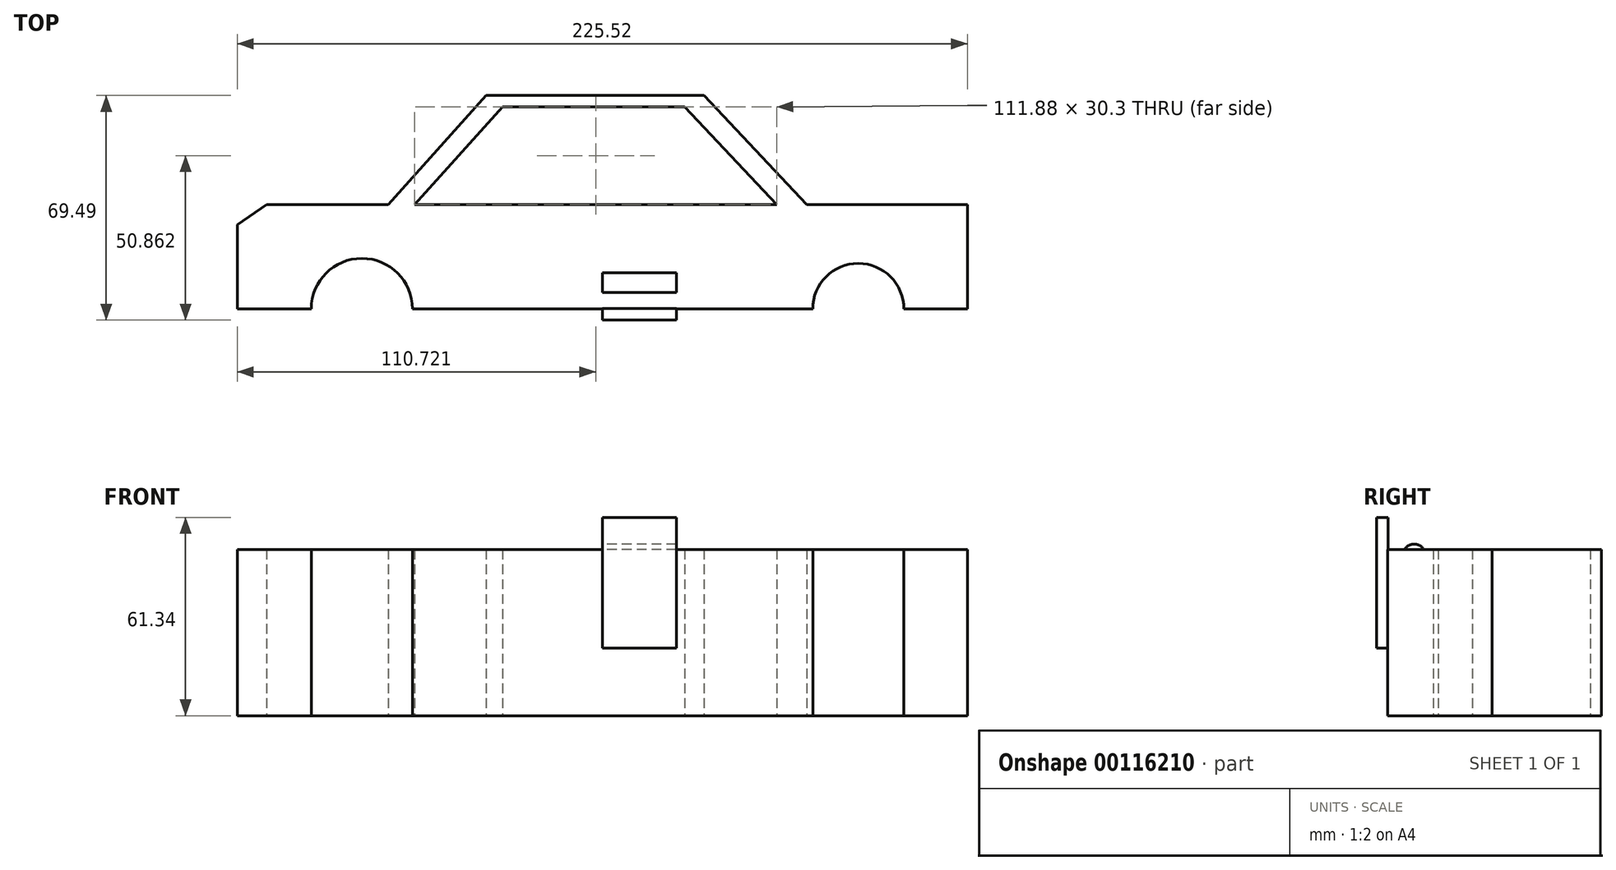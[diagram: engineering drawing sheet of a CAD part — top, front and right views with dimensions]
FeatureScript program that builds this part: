
annotation { "Feature Type Name" : "Feature", "Feature Type Description" : "" }
export const myFeature = defineFeature(function(context is Context, id is Id, definition is map)
    precondition{}
    {
        {
            var Q0;
            Q0=qCreatedBy(makeId("Top.planeOp"),FACE);
            var sketch = newSketch(context, id + "F0", { "sketchPlane" : qUnion([Q0])});
            skLineSegment(sketch, "E0.bottom", {"start": v(112.76, -16.11) * mm, "end": v(-58.65, -16.11) * mm});
            skLineSegment(sketch, "E0.top", {"start": v(112.76, 16.11) * mm, "end": v(-103.69, 16.11) * mm});
            skLineSegment(sketch, "E0.left", {"start": v(112.76, -16.11) * mm, "end": v(112.76, 16.11) * mm});
            skLineSegment(sketch, "E0.right", {"start": v(-112.76, -16.11) * mm, "end": v(-112.76, 9.97) * mm});
            skPoint(sketch, "E0.middle", {"position": v(0, 0) * mm});
            skCircle(sketch, "E1", {"center": v(79.08, -16.11) * mm, "radius": 14.07 * mm});
            skLineSegment(sketch, "E2", {"start": v(-35.85, 49.89) * mm, "end": v(31.41, 49.89) * mm});
            skLineSegment(sketch, "E3", {"start": v(31.41, 49.89) * mm, "end": v(63.17, 16.11) * mm});
            skLineSegment(sketch, "E4", {"start": v(-35.85, 49.89) * mm, "end": v(-66.1, 16.11) * mm});
            skLineSegment(sketch, "E5", {"start": v(-103.69, 16.11) * mm, "end": v(-112.76, 9.97) * mm});
            skPoint(sketch, "E5.endSnap0", {"position": v(-112.76, 0) * mm});
            skLineSegment(sketch, "E6", {"start": v(-38.96, 46.41) * mm, "end": v(34.68, 46.41) * mm});
            skLineSegment(sketch, "E7", {"start": v(-27.73, 49.89) * mm, "end": v(-57.98, 16.11) * mm});
            skLineSegment(sketch, "E8", {"start": v(22.14, 49.89) * mm, "end": v(53.9, 16.11) * mm});
            skLineSegment(sketch, "E9", {"start": v(0, 46.41) * mm, "end": v(0, -16.11) * mm});
            skArc(sketch, "E10", {"start": v(-53.87, -16.11) * mm, "mid": v(-54.92, -9.64) * mm, "end": v(-57.98, -3.83) * mm});
            skLineSegment(sketch, "E11", {"start": v(-57.98, 16.11) * mm, "end": v(-57.98, -3.83) * mm});
            skLineSegment(sketch, "E12", {"start": v(53.9, 16.11) * mm, "end": v(53.9, -16.11) * mm});
            skPoint(sketch, "E13.orphan", {"position": v(-112.76, 16.11) * mm});
            skPoint(sketch, "E14.orphan", {"position": v(-127.5, 0) * mm});
            skArc(sketch, "E15", {"start": v(-58.65, -16.11) * mm, "mid": v(-74.28, -0.48) * mm, "end": v(-89.91, -16.11) * mm});
            skCircle(sketch, "E16", {"center": v(-74.28, -16.11) * mm, "radius": 8.72 * mm});
            skLineSegment(sketch, "E17.trimOffspring", {"start": v(-89.91, -16.11) * mm, "end": v(-112.76, -16.11) * mm});
            skCircle(sketch, "E18", {"center": v(-74.28, -16.11) * mm, "radius": 12.8 * mm});
            skCircle(sketch, "E19", {"center": v(-74.28, -16.11) * mm, "radius": 3.66 * mm});
            skSolve(sketch);
        }
        {
            var Q0;
            {var subQ0=sQuery(id+"F0.wireOp",EDGE,"E10");Q0=makeQuery(id+"F0.imprint","IMPRINT",FACE,{"disambiguationData":[TD([[makeQuery(id+"F0.imprint","IMPRINT",EDGE,{"derivedFrom":subQ0}),-1.0]])]});}
            var Q1;
            {var subQ3=sQuery(id+"F0.wireOp",EDGE,"E12");Q1=makeQuery(id+"F0.imprint","IMPRINT",FACE,{"disambiguationData":[TD([[makeQuery(id+"F0.imprint","IMPRINT",EDGE,{"derivedFrom":subQ3}),-1.0]])]});}
            var Q2;
            {var subQ0=sQuery(id+"F0.wireOp",EDGE,"E4");var subQ1=sQuery(id+"F0.wireOp",EDGE,"E0.top");var subQ2=makeQuery(id+"F0.imprint","INTERSECT",VERTEX,{"derivedFrom":[subQ1,subQ0]});Q2=makeQuery(id+"F0.imprint","IMPRINT",FACE,{"disambiguationData":[TD([[makeQuery(id+"F0.imprint","IMPRINT",EDGE,{"disambiguationData":[TD([[subQ2,1.0]])],"derivedFrom":subQ0}),1.0]])]});}
            var Q3;
            {var subQ0=sQuery(id+"F0.wireOp",EDGE,"E4");var subQ1=sQuery(id+"F0.wireOp",EDGE,"E2");var subQ2=makeQuery(id+"F0.imprint","INTERSECT",VERTEX,{"derivedFrom":[subQ1,subQ0]});Q3=makeQuery(id+"F0.imprint","IMPRINT",FACE,{"disambiguationData":[TD([[makeQuery(id+"F0.imprint","IMPRINT",EDGE,{"disambiguationData":[TD([[subQ2,-1.0]])],"derivedFrom":subQ1}),-1.0]])]});}
            var Q4;
            {var subQ0=sQuery(id+"F0.wireOp",EDGE,"E7");var subQ1=sQuery(id+"F0.wireOp",EDGE,"E2");var subQ2=makeQuery(id+"F0.imprint","INTERSECT",VERTEX,{"derivedFrom":[subQ1,subQ0]});Q4=makeQuery(id+"F0.imprint","IMPRINT",FACE,{"disambiguationData":[TD([[makeQuery(id+"F0.imprint","IMPRINT",EDGE,{"disambiguationData":[TD([[subQ2,-1.0]])],"derivedFrom":subQ1}),-1.0]])]});}
            var Q5;
            {var subQ0=sQuery(id+"F0.wireOp",EDGE,"E3");var subQ1=sQuery(id+"F0.wireOp",EDGE,"E2");var subQ2=makeQuery(id+"F0.imprint","INTERSECT",VERTEX,{"derivedFrom":[subQ1,subQ0]});Q5=makeQuery(id+"F0.imprint","IMPRINT",FACE,{"disambiguationData":[TD([[makeQuery(id+"F0.imprint","IMPRINT",EDGE,{"disambiguationData":[TD([[subQ2,1.0]])],"derivedFrom":subQ1}),-1.0]])]});}
            var Q6;
            {var subQ0=sQuery(id+"F0.wireOp",EDGE,"E3");var subQ1=sQuery(id+"F0.wireOp",EDGE,"E0.top");var subQ2=makeQuery(id+"F0.imprint","INTERSECT",VERTEX,{"derivedFrom":[subQ1,subQ0]});Q6=makeQuery(id+"F0.imprint","IMPRINT",FACE,{"disambiguationData":[TD([[makeQuery(id+"F0.imprint","IMPRINT",EDGE,{"disambiguationData":[TD([[subQ2,1.0]])],"derivedFrom":subQ0}),-1.0]])]});}
            var Q7;
            {var subQ0=sQuery(id+"F0.wireOp",EDGE,"E0.left");Q7=makeQuery(id+"F0.imprint","IMPRINT",FACE,{"disambiguationData":[TD([[makeQuery(id+"F0.imprint","IMPRINT",EDGE,{"derivedFrom":subQ0}),1.0]])]});}
            var Q8;
            Q8=makeQuery(id+"F0.imprint","IMPRINT",FACE,{"disambiguationData":[TD([[makeQuery(id+"F0.imprint","IMPRINT",EDGE,{"derivedFrom":sQuery(id+"F0.wireOp",EDGE,"E0.right")}),-1.0]])]});
            extrude(context, id + "F1", {"entities" : qUnion([Q0, Q1, Q2, Q3, Q4, Q5, Q6, Q7, Q8]), "depth" : 0.06 * yard});
        }
        {
            var Q0;
            Q0=qCreatedBy(makeId("Right.planeOp"),FACE);
            var sketch = newSketch(context, id + "F2", { "sketchPlane" : qUnion([Q0])});
            skLineSegment(sketch, "E20.bottom", {"start": v(-13.8, 52.65) * mm, "end": v(4.89, 52.65) * mm});
            skLineSegment(sketch, "E20.top", {"start": v(-13.8, 28.09) * mm, "end": v(4.89, 28.09) * mm});
            skLineSegment(sketch, "E20.left", {"start": v(-13.8, 52.65) * mm, "end": v(-13.8, 28.09) * mm});
            skLineSegment(sketch, "E20.right", {"start": v(4.89, 52.65) * mm, "end": v(4.89, 28.09) * mm});
            skPoint(sketch, "E20.middle", {"position": v(-4.46, 40.37) * mm});
            skCircle(sketch, "E21", {"center": v(0, 21.87) * mm, "radius": 4.97 * mm});
            skCircle(sketch, "E22", {"center": v(0, 59.96) * mm, "radius": 3.66 * mm});
            skLineSegment(sketch, "E23", {"start": v(4.89, 28.09) * mm, "end": v(-2.46, 28.09) * mm});
            skLineSegment(sketch, "E24", {"start": v(4.89, 40.37) * mm, "end": v(-13.8, 40.37) * mm});
            skLineSegment(sketch, "E25", {"start": v(4.89, 46.5) * mm, "end": v(-13.8, 46.5) * mm});
            skLineSegment(sketch, "E26", {"start": v(4.89, 32.74) * mm, "end": v(-13.8, 32.74) * mm});
            skLineSegment(sketch, "E27", {"start": v(4.89, 36.42) * mm, "end": v(-13.8, 36.42) * mm});
            skLineSegment(sketch, "E28", {"start": v(4.89, 46.5) * mm, "end": v(-2.25, 46.5) * mm});
            skLineSegment(sketch, "E29", {"start": v(4.89, 49.85) * mm, "end": v(-13.8, 49.85) * mm});
            skLineSegment(sketch, "E30", {"start": v(4.89, 43.23) * mm, "end": v(-13.8, 43.23) * mm});
            skLineSegment(sketch, "E31.bottom", {"start": v(-19.6, 61.34) * mm, "end": v(-16, 61.34) * mm});
            skLineSegment(sketch, "E31.top", {"start": v(-19.6, 20.95) * mm, "end": v(-16, 20.95) * mm});
            skLineSegment(sketch, "E31.left", {"start": v(-19.6, 61.34) * mm, "end": v(-19.6, 20.95) * mm});
            skLineSegment(sketch, "E31.right", {"start": v(-16, 61.34) * mm, "end": v(-16, 20.95) * mm});
            skPoint(sketch, "E31.middle", {"position": v(-17.8, 41.15) * mm});
            skSolve(sketch);
        }
        {
            var Q0;
            Q0=makeQuery(id+"F2.imprint","IMPRINT",FACE,{"disambiguationData":[TD([[makeQuery(id+"F2.imprint","IMPRINT",EDGE,{"derivedFrom":sQuery(id+"F2.wireOp",EDGE,"E31.bottom")}),-1.0]])]});
            extrude(context, id + "F3", {"entities" : qUnion([Q0]), "operationType" : NewBodyOperationType.ADD, "depth" : 0.03 * yard});
        }
        {
            var Q0;
            Q0=qCreatedBy(makeId("Right.planeOp"),FACE);
            var sketch = newSketch(context, id + "F4", { "sketchPlane" : qUnion([Q0])});
            skCircle(sketch, "E32", {"center": v(-9.16, 17.24) * mm, "radius": 4.15 * mm});
            skCircle(sketch, "E33", {"center": v(-7.95, 49.54) * mm, "radius": 3.56 * mm});
            skSolve(sketch);
        }
        {
            var Q0;
            Q0 = qSketchRegion(id + "F4", true);
            extrude(context, id + "F5", {"entities" : qUnion([Q0]), "operationType" : NewBodyOperationType.ADD, "depth" : 0.03 * yard});
        }
    });
